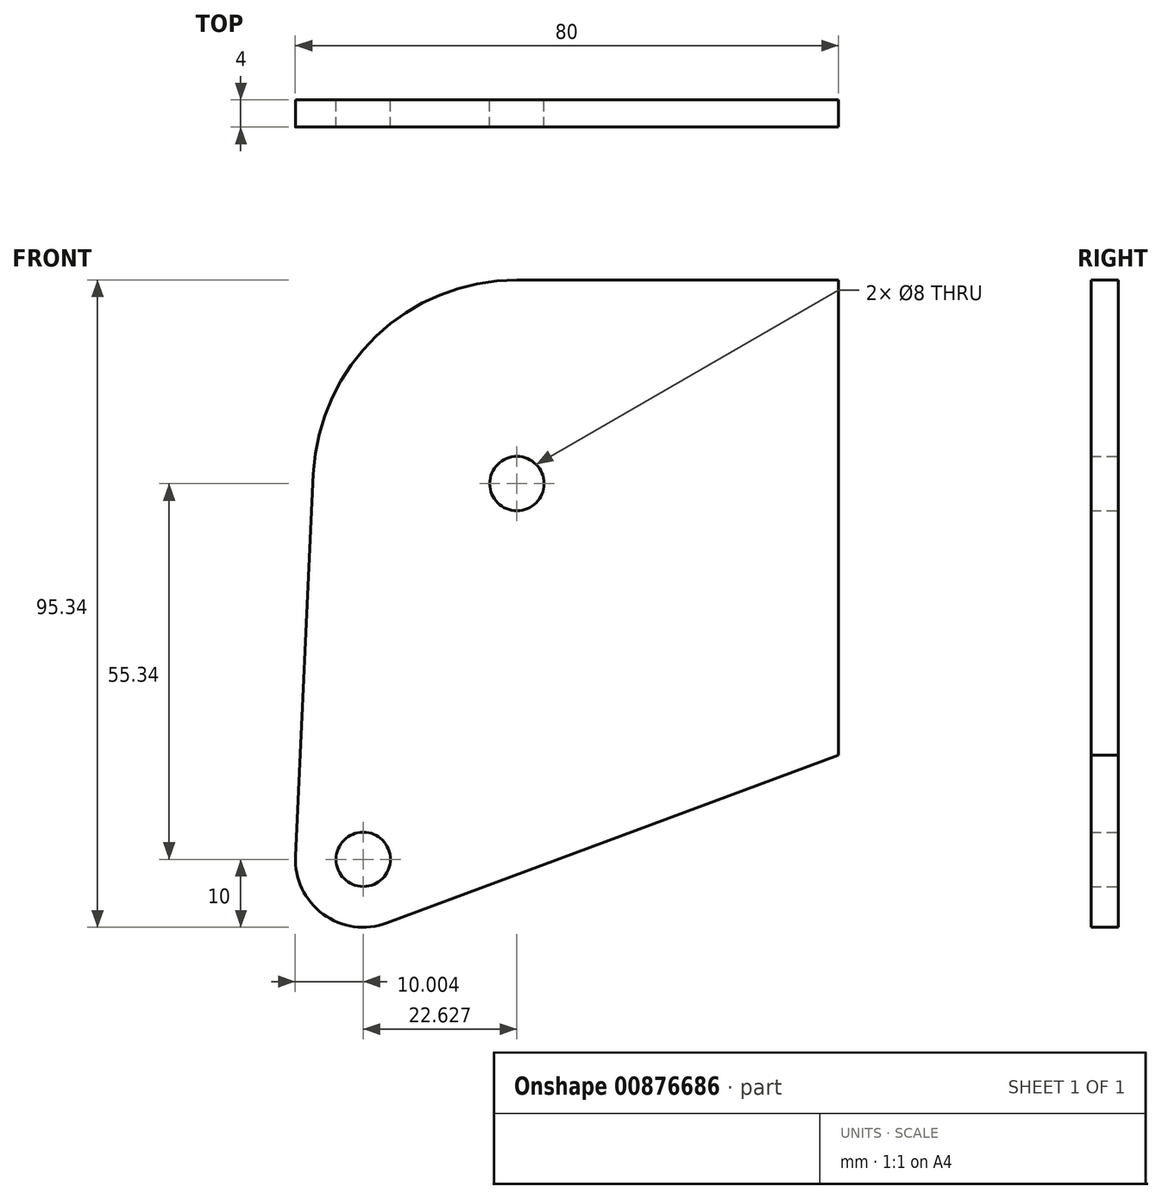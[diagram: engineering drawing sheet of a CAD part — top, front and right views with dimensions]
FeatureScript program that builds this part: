
annotation { "Feature Type Name" : "Feature", "Feature Type Description" : "" }
export const myFeature = defineFeature(function(context is Context, id is Id, definition is map)
    precondition{}
    {
        {
            var Q0;
            Q0=qCreatedBy(makeId("Front.planeOp"),FACE);
            var sketch = newSketch(context, id + "F0", { "sketchPlane" : qUnion([Q0])});
            skCircle(sketch, "E0", {"center": v(0, 0) * mm, "radius": 4 * mm});
            skLineSegment(sketch, "E1.trimOffspring", {"start": v(0, 4) * mm, "end": v(0, -4) * mm});
            skCircle(sketch, "E2", {"center": v(-22.63, -55.34) * mm, "radius": 4 * mm});
            skArc(sketch, "E3", {"start": v(-32.62, -54.87) * mm, "mid": v(-28.53, -63.41) * mm, "end": v(-19.14, -64.71) * mm});
            skArc(sketch, "E4", {"start": v(0, 30) * mm, "mid": v(-20.7, 21.7) * mm, "end": v(-29.97, 1.41) * mm});
            skLineSegment(sketch, "E5", {"start": v(-32.62, -54.87) * mm, "end": v(-29.97, 1.41) * mm});
            skLineSegment(sketch, "E6", {"start": v(47.37, -40) * mm, "end": v(47.37, 30) * mm});
            skLineSegment(sketch, "E7", {"start": v(0, 30) * mm, "end": v(47.37, 30) * mm});
            skLineSegment(sketch, "E8", {"start": v(-19.14, -64.71) * mm, "end": v(47.37, -40) * mm});
            skSolve(sketch);
        }
        {
            var Q0;
            Q0 = qSketchRegion(id + "F0", true);
            extrude(context, id + "F1", {"entities" : qUnion([Q0]), "depth" : 4 * mm, "offsetDistance" : 25 * mm});
        }
    });
